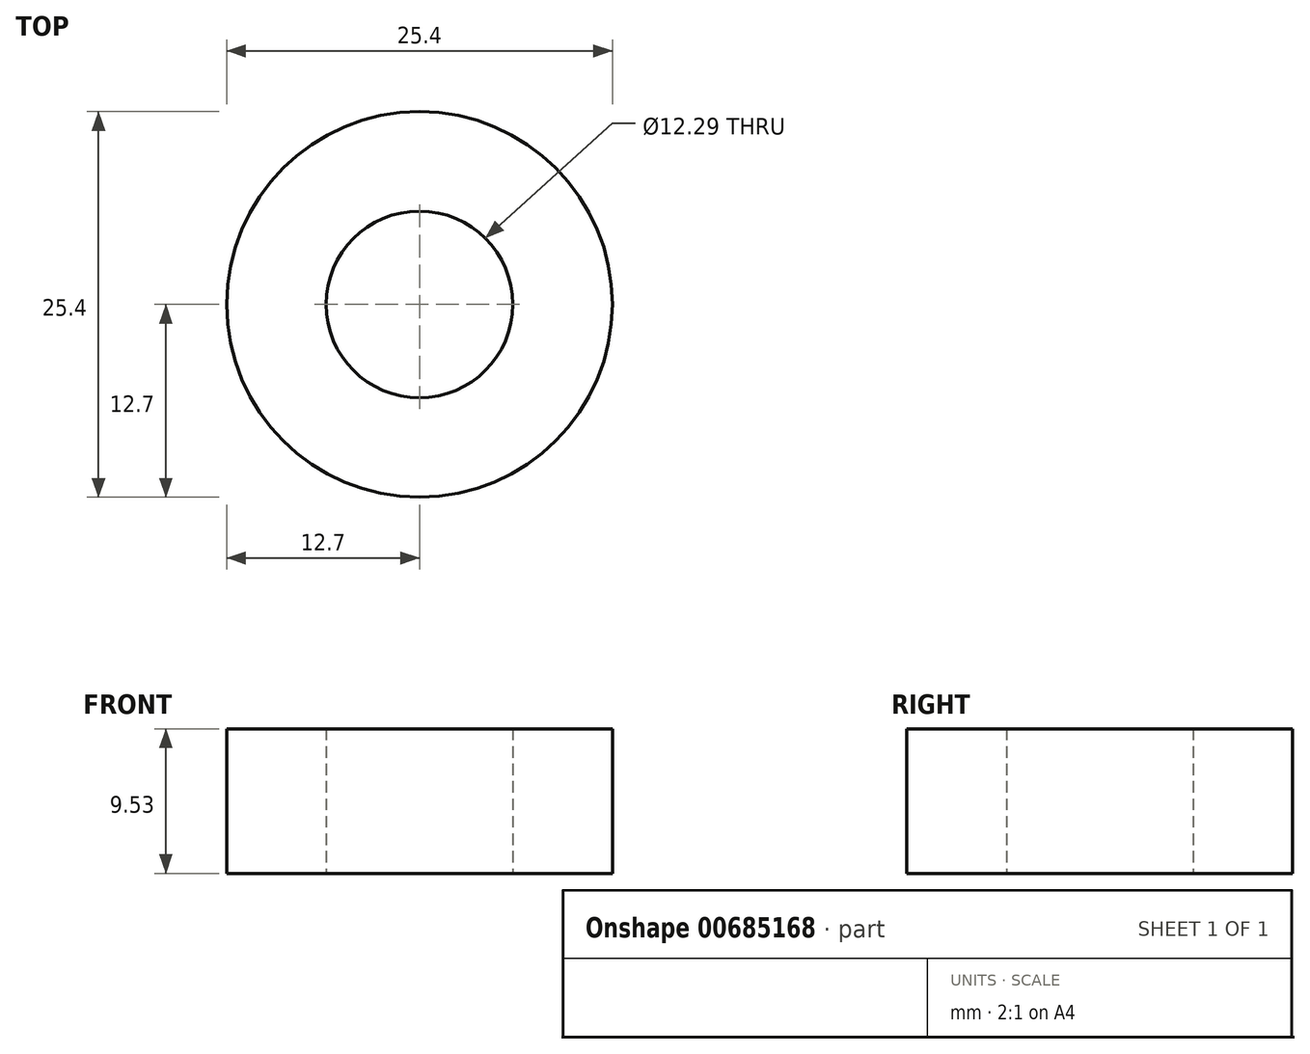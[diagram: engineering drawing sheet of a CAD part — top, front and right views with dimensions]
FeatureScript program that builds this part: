
annotation { "Feature Type Name" : "Feature", "Feature Type Description" : "" }
export const myFeature = defineFeature(function(context is Context, id is Id, definition is map)
    precondition{}
    {
        {
            var Q0;
            Q0=qCreatedBy(makeId("Top.planeOp"),FACE);
            var sketch = newSketch(context, id + "F0", { "sketchPlane" : qUnion([Q0])});
            skCircle(sketch, "E0", {"center": v(0, 0) * mm, "radius": 6.14 * mm});
            skCircle(sketch, "E1", {"center": v(0, 0) * mm, "radius": 12.7 * mm});
            skSolve(sketch);
        }
        {
            var Q0;
            Q0 = qSketchRegion(id + "F0", true);
            extrude(context, id + "F1", {"entities" : qUnion([Q0]), "depth" : 9.52 * mm, "offsetDistance" : 25.4 * mm});
        }
    });
